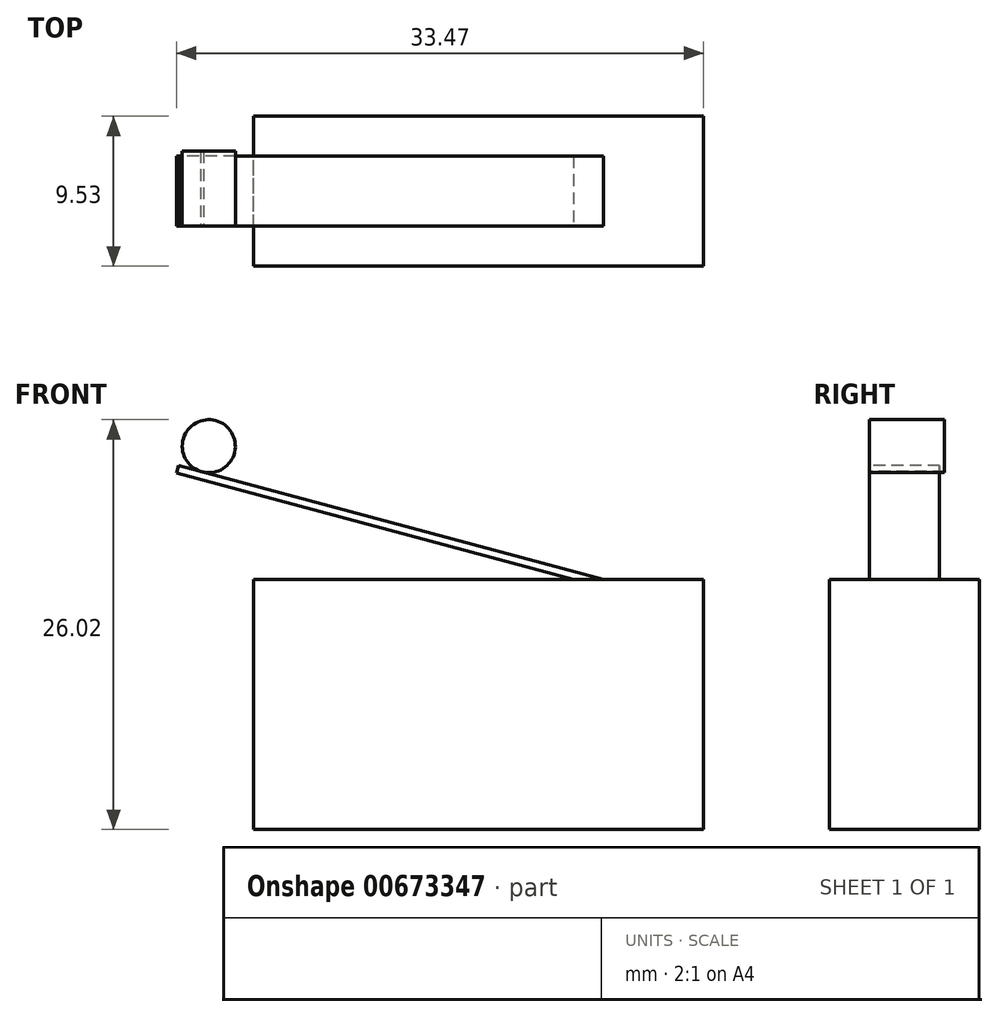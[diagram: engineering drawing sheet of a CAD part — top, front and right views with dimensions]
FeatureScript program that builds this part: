
annotation { "Feature Type Name" : "Feature", "Feature Type Description" : "" }
export const myFeature = defineFeature(function(context is Context, id is Id, definition is map)
    precondition{}
    {
        {
            var Q0;
            Q0=qCreatedBy(makeId("Front.planeOp"),FACE);
            var sketch = newSketch(context, id + "F0", { "sketchPlane" : qUnion([Q0])});
            skLineSegment(sketch, "E0.bottom", {"start": v(-14.29, 7.94) * mm, "end": v(14.29, 7.94) * mm});
            skLineSegment(sketch, "E0.top", {"start": v(-14.29, -7.94) * mm, "end": v(14.29, -7.94) * mm});
            skLineSegment(sketch, "E0.left", {"start": v(-14.29, 7.94) * mm, "end": v(-14.29, -7.94) * mm});
            skLineSegment(sketch, "E0.right", {"start": v(14.29, 7.94) * mm, "end": v(14.29, -7.94) * mm});
            skPoint(sketch, "E0.middle", {"position": v(0, 0) * mm});
            skSolve(sketch);
        }
        {
            var Q0;
            Q0=makeQuery(id+"F0.imprint","IMPRINT",FACE,{"disambiguationData":[TD([[makeQuery(id+"F0.imprint","IMPRINT",EDGE,{"derivedFrom":sQuery(id+"F0.wireOp",EDGE,"E0.bottom")}),-1.0]])]});
            extrude(context, id + "F1", {"entities" : qUnion([Q0]), "depth" : 9.52 * mm, "offsetDistance" : 25.4 * mm});
        }
        {
            var Q0;
            Q0=makeQuery(id+"F1.opExtrude","CAP_FACE",FACE,{"disambiguationData":[OSD([sQuery(id+"F0.wireOp",EDGE,"E0.bottom"),sQuery(id+"F0.wireOp",EDGE,"E0.top"),sQuery(id+"F0.wireOp",EDGE,"E0.left"),sQuery(id+"F0.wireOp",EDGE,"E0.right")])],"isStart":false});
            var sketch = newSketch(context, id + "F2", { "sketchPlane" : qUnion([Q0])});
            skLineSegment(sketch, "E1", {"start": v(6.03, 7.94) * mm, "end": v(-19.18, 14.7) * mm});
            skLineSegment(sketch, "E2", {"start": v(-19.18, 14.7) * mm, "end": v(-19.05, 15.17) * mm});
            skLineSegment(sketch, "E3", {"start": v(-19.05, 15.17) * mm, "end": v(7.94, 7.94) * mm});
            skLineSegment(sketch, "E4", {"start": v(7.94, 7.94) * mm, "end": v(6.03, 7.94) * mm});
            skSolve(sketch);
        }
        {
            var Q0;
            Q0 = qSketchRegion(id + "F2", true);
            var Q1;
            Q1=makeQuery(id+"F1.opExtrude","CAP_FACE",FACE,{"disambiguationData":[OSD([sQuery(id+"F0.wireOp",EDGE,"E0.bottom"),sQuery(id+"F0.wireOp",EDGE,"E0.top"),sQuery(id+"F0.wireOp",EDGE,"E0.left"),sQuery(id+"F0.wireOp",EDGE,"E0.right")])],"isStart":true});
            var Q2;
            Q2=makeQuery(id+"F1.opExtrude","CAP_FACE",FACE,{"disambiguationData":[OSD([sQuery(id+"F0.wireOp",EDGE,"E0.bottom"),sQuery(id+"F0.wireOp",EDGE,"E0.top"),sQuery(id+"F0.wireOp",EDGE,"E0.left"),sQuery(id+"F0.wireOp",EDGE,"E0.right")])],"isStart":true});
            extrude(context, id + "F3", {"entities" : qUnion([Q0]), "endBound" : BoundingType.UP_TO_SURFACE, "oppositeDirection" : true, "depth" : 4.76 * mm, "endBoundEntityFace" : qUnion([Q1]), "hasOffset" : true, "offsetDistance" : 2.54 * mm, "hasSecondDirection" : true, "secondDirectionOppositeDirection" : false, "secondDirectionDepth" : -2.54 * mm, "secondDirectionBoundEntityFace" : qUnion([Q2])});
        }
        {
            var Q0;
            Q0=makeQuery(id+"F3.opExtrude","CAP_FACE",FACE,{"disambiguationData":[OSD([sQuery(id+"F2.wireOp",EDGE,"E1"),sQuery(id+"F2.wireOp",EDGE,"E2"),sQuery(id+"F2.wireOp",EDGE,"E3"),sQuery(id+"F2.wireOp",EDGE,"E4")])],"isStart":true});
            var sketch = newSketch(context, id + "F4", { "sketchPlane" : qUnion([Q0])});
            skCircle(sketch, "E5", {"center": v(-17.14, 16.4) * mm, "radius": 1.68 * mm});
            skPoint(sketch, "E5.first.point", {"position": v(-18.59, 17.25) * mm});
            skPoint(sketch, "E5.second.point", {"position": v(-15.61, 15.67) * mm});
            skPoint(sketch, "E5.third.point", {"position": v(-17.67, 14.8) * mm});
            skSolve(sketch);
        }
        {
            var Q0;
            {var subQ0=sQuery(id+"F4.wireOp",EDGE,"E5");var subQ1=makeQuery(id+"F3.opExtrude","CAP_EDGE",EDGE,{"disambiguationData":[OSD([sQuery(id+"F2.wireOp",EDGE,"E3")])],"isStart":true});var subQ2=makeQuery(id+"F4.imprint","INTERSECT",VERTEX,{"disambiguationData":[OD(0.0)],"derivedFrom":[subQ1,subQ0]});Q0=makeQuery(id+"F4.imprint","IMPRINT",FACE,{"disambiguationData":[TD([[makeQuery(id+"F4.imprint","IMPRINT",EDGE,{"disambiguationData":[TD([[subQ2,1.0]])],"derivedFrom":subQ0}),1.0]])]});}
            extrude(context, id + "F5", {"entities" : qUnion([Q0]), "depth" : -4.76 * mm, "offsetDistance" : 25.4 * mm});
        }
    });
